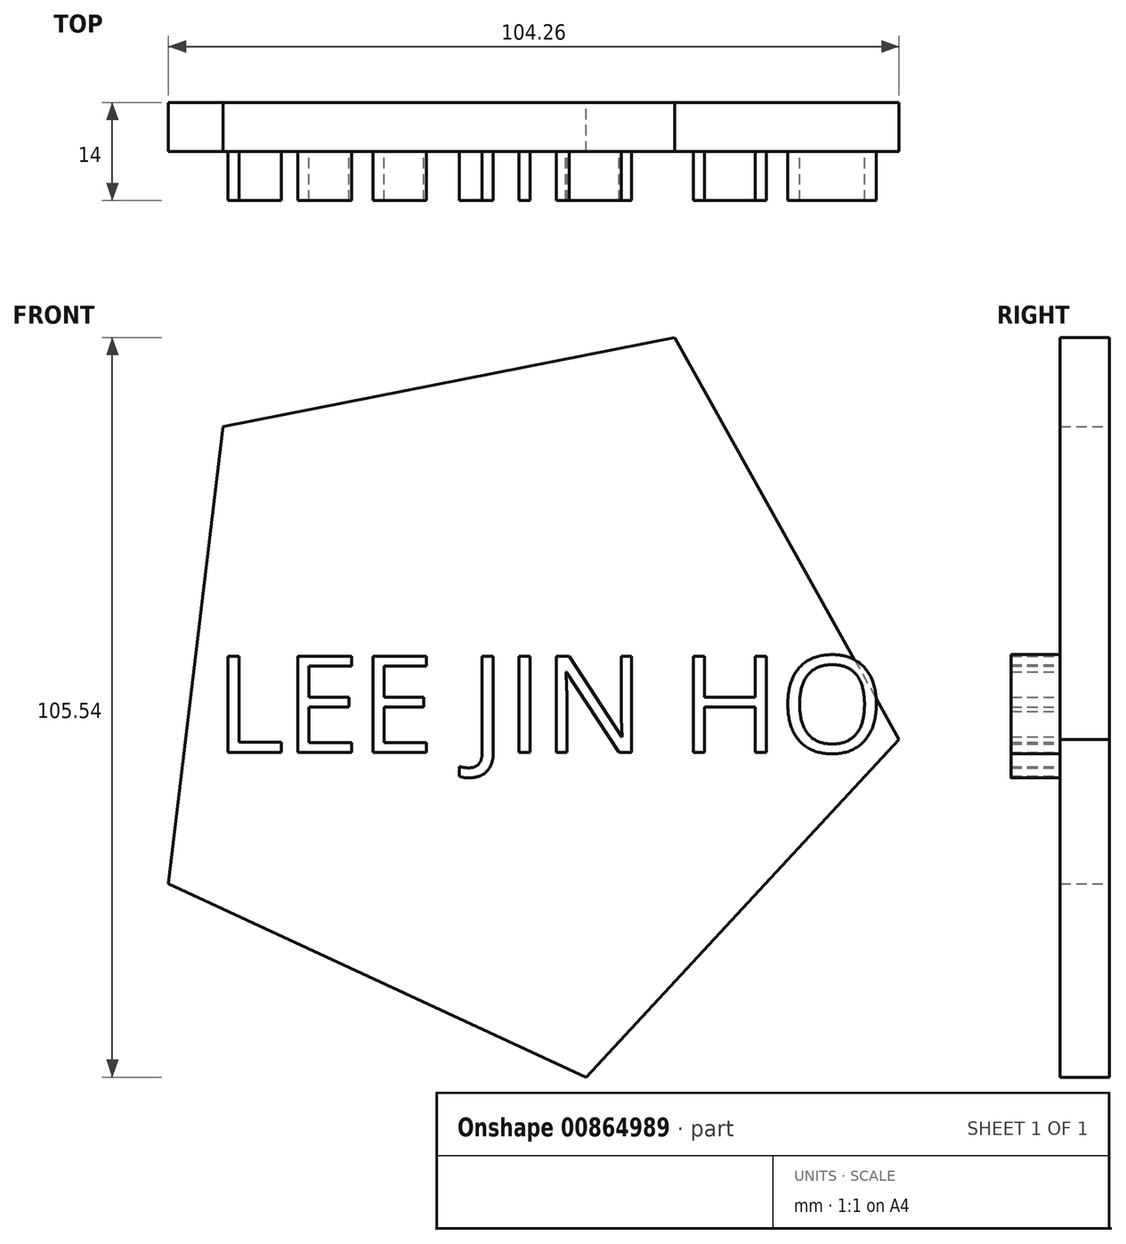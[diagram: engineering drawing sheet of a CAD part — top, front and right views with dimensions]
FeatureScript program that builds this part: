
annotation { "Feature Type Name" : "Feature", "Feature Type Description" : "" }
export const myFeature = defineFeature(function(context is Context, id is Id, definition is map)
    precondition{}
    {
        {
            var Q0;
            Q0=qCreatedBy(makeId("Front.planeOp"),FACE);
            var sketch = newSketch(context, id + "F0", { "sketchPlane" : qUnion([Q0])});
            skCircle(sketch, "E0.cCircle", {"center": v(0, 0) * mm, "radius": 45.2 * mm, "construction": true});
            skLineSegment(sketch, "E0.0", {"start": v(23.45, 50.72) * mm, "end": v(55.48, -6.63) * mm});
            skLineSegment(sketch, "E0.1", {"start": v(55.48, -6.63) * mm, "end": v(10.84, -54.82) * mm});
            skLineSegment(sketch, "E0.2", {"start": v(10.84, -54.82) * mm, "end": v(-48.78, -27.25) * mm});
            skLineSegment(sketch, "E0.3", {"start": v(-48.78, -27.25) * mm, "end": v(-41, 37.97) * mm});
            skLineSegment(sketch, "E0.4", {"start": v(-41, 37.97) * mm, "end": v(23.45, 50.72) * mm});
            skPoint(sketch, "E0.0.midPoint", {"position": v(39.47, 22.05) * mm});
            skSolve(sketch);
        }
        {
            var Q0;
            Q0=makeQuery(id+"F0.imprint","IMPRINT",FACE,{"disambiguationData":[TD([[makeQuery(id+"F0.imprint","IMPRINT",EDGE,{"derivedFrom":sQuery(id+"F0.wireOp",EDGE,"E0.0")}),-1.0]])]});
            extrude(context, id + "F1", {"entities" : qUnion([Q0]), "depth" : 7 * mm, "offsetDistance" : 25 * mm});
        }
        {
            var Q0;
            Q0=makeQuery(id+"F1.opExtrude","CAP_FACE",FACE,{"disambiguationData":[OSD([sQuery(id+"F0.wireOp",EDGE,"E0.0"),sQuery(id+"F0.wireOp",EDGE,"E0.1"),sQuery(id+"F0.wireOp",EDGE,"E0.2"),sQuery(id+"F0.wireOp",EDGE,"E0.3"),sQuery(id+"F0.wireOp",EDGE,"E0.4")])],"isStart":false});
            var sketch = newSketch(context, id + "F2", { "sketchPlane" : qUnion([Q0])});
            skText(sketch, "E1", { "text": "LEE JIN HO", "fontName": "OpenSans-Regular.ttf"});
            skPoint(sketch, "E1.secondSnap0", {"position": v(-44.89, 5.36) * mm});
            const initialGuessF2  = {"E1": [-0.0422, -0.0085, 1, 0, 0.01386]};
            skSetInitialGuess(sketch, initialGuessF2);
            skSolve(sketch);
        }
        {
            var Q0;
            Q0 = qSketchRegion(id + "F2", true);
            extrude(context, id + "F3", {"entities" : qUnion([Q0]), "operationType" : NewBodyOperationType.ADD, "depth" : 7 * mm, "offsetDistance" : 25 * mm});
        }
    });
